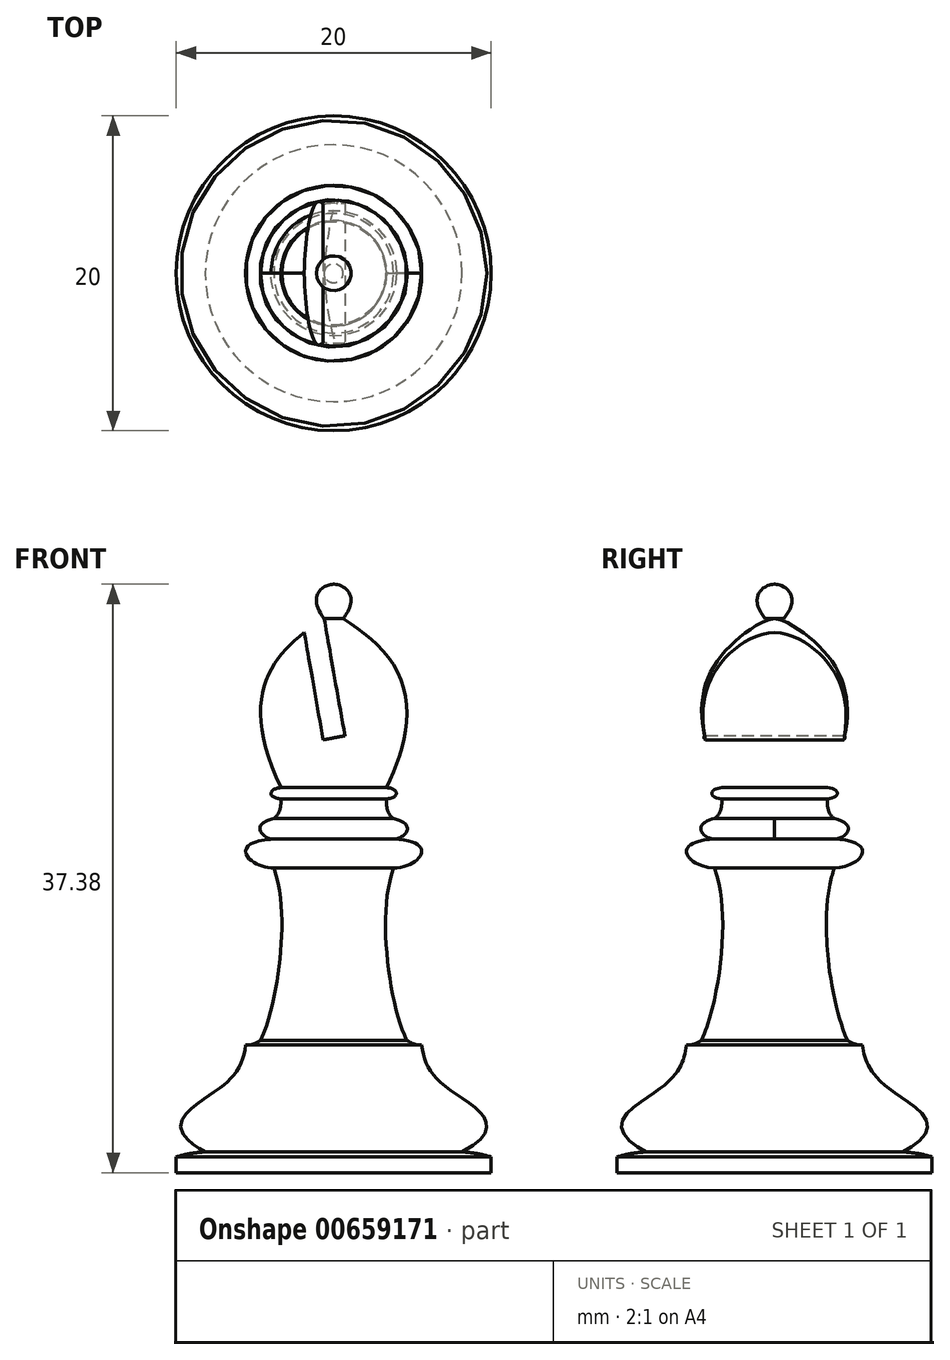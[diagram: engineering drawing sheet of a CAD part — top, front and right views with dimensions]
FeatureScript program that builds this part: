
annotation { "Feature Type Name" : "Feature", "Feature Type Description" : "" }
export const myFeature = defineFeature(function(context is Context, id is Id, definition is map)
    precondition{}
    {
        {
            var Q0;
            Q0=qCreatedBy(makeId("Front.planeOp"),FACE);
            var sketch = newSketch(context, id + "F0", { "sketchPlane" : qUnion([Q0])});
            skSolve(sketch);
        }
        {
            var Q0;
            Q0=qCreatedBy(makeId("Front.planeOp"),FACE);
            var sketch = newSketch(context, id + "F1", { "sketchPlane" : qUnion([Q0])});
            skLineSegment(sketch, "E0", {"start": v(0, 0) * mm, "end": v(-10, 0) * mm});
            skLineSegment(sketch, "E1", {"start": v(-10, 0) * mm, "end": v(-10, 1) * mm});
            skFitSpline(sketch, "E2", {"points": [v(-10, 1) * mm, v(-8.16, 1.31) * mm], "startDerivative": vector(1.97, 0.59) * mm, "endDerivative": vector(1.85, 0.07) * mm});
            skFitSpline(sketch, "E3", {"points": [v(-8.16, 1.31) * mm, v(-7.46, 5.2) * mm, v(-5.6, 8.1) * mm], "startDerivative": vector(-18.59, 9.88) * mm, "endDerivative": vector(0.78, 7.08) * mm});
            skFitSpline(sketch, "E4", {"points": [v(-5.6, 8.1) * mm, v(-4.63, 8.41) * mm], "startDerivative": vector(0.94, -0.1) * mm, "endDerivative": vector(0.9, 0.62) * mm});
            skFitSpline(sketch, "E5", {"points": [v(-4.63, 8.41) * mm, v(-3.8, 19.34) * mm], "startDerivative": vector(3.34, 7) * mm, "endDerivative": vector(-3.23, 8.6) * mm});
            skFitSpline(sketch, "E6", {"points": [v(-3.8, 19.34) * mm, v(-3.8, 21.18) * mm], "startDerivative": vector(-5.42, 0.26) * mm, "endDerivative": vector(8.7, 0.27) * mm});
            skFitSpline(sketch, "E7", {"points": [v(-3.8, 21.18) * mm, v(-3.8, 22.5) * mm], "startDerivative": vector(-1.96, 0) * mm, "endDerivative": vector(4.84, 1.22) * mm});
            skFitSpline(sketch, "E8", {"points": [v(-3.8, 22.5) * mm, v(-3.35, 23.74) * mm], "startDerivative": vector(1.17, 0.74) * mm, "endDerivative": vector(-0.04, 1.5) * mm});
            skFitSpline(sketch, "E9", {"points": [v(-3.35, 23.74) * mm, v(-3.35, 24.45) * mm], "startDerivative": vector(-3, 0.38) * mm, "endDerivative": vector(2.03, 0.04) * mm});
            skFitSpline(sketch, "E10", {"points": [v(-3.35, 24.45) * mm, v(-0.6, 35.2) * mm], "startDerivative": vector(-9.02, 18.72) * mm, "endDerivative": vector(9, 5.83) * mm});
            skFitSpline(sketch, "E11", {"points": [v(-0.6, 35.2) * mm, v(0, 37.38) * mm], "startDerivative": vector(-3.4, 4.2) * mm, "endDerivative": vector(2.11, -0.03) * mm});
            skLineSegment(sketch, "E12", {"start": v(0, 37.38) * mm, "end": v(0, 0) * mm});
            skSolve(sketch);
        }
        {
            var Q0;
            Q0 = qSketchRegion(id + "F1", true);
            var Q1;
            Q1=sQuery(id+"F1.wireOp",EDGE,"E12");
            revolve(context, id + "F2", {"entities" : qUnion([Q0]), "axis" : qUnion([Q1]), "revolveType" : RevolveType.FULL});
        }
        {
            var Q0;
            Q0=qCreatedBy(makeId("Front.planeOp"),FACE);
            var sketch = newSketch(context, id + "F3", { "sketchPlane" : qUnion([Q0])});
            skLineSegment(sketch, "E13", {"start": v(-0.6, 35.2) * mm, "end": v(-1.98, 34.95) * mm});
            skLineSegment(sketch, "E14", {"start": v(-1.98, 34.95) * mm, "end": v(-0.67, 27.5) * mm});
            skLineSegment(sketch, "E15", {"start": v(-0.67, 27.5) * mm, "end": v(0.71, 27.74) * mm});
            skLineSegment(sketch, "E16", {"start": v(0.71, 27.74) * mm, "end": v(-0.6, 35.2) * mm});
            skSolve(sketch);
        }
        {
            var Q0;
            Q0 = qSketchRegion(id + "F3", true);
            extrude(context, id + "F4", {"entities" : qUnion([Q0]), "operationType" : NewBodyOperationType.REMOVE, "endBound" : BoundingType.SYMMETRIC, "oppositeDirection" : true, "depth" : 50 * mm, "offsetDistance" : 25 * mm});
        }
    });
